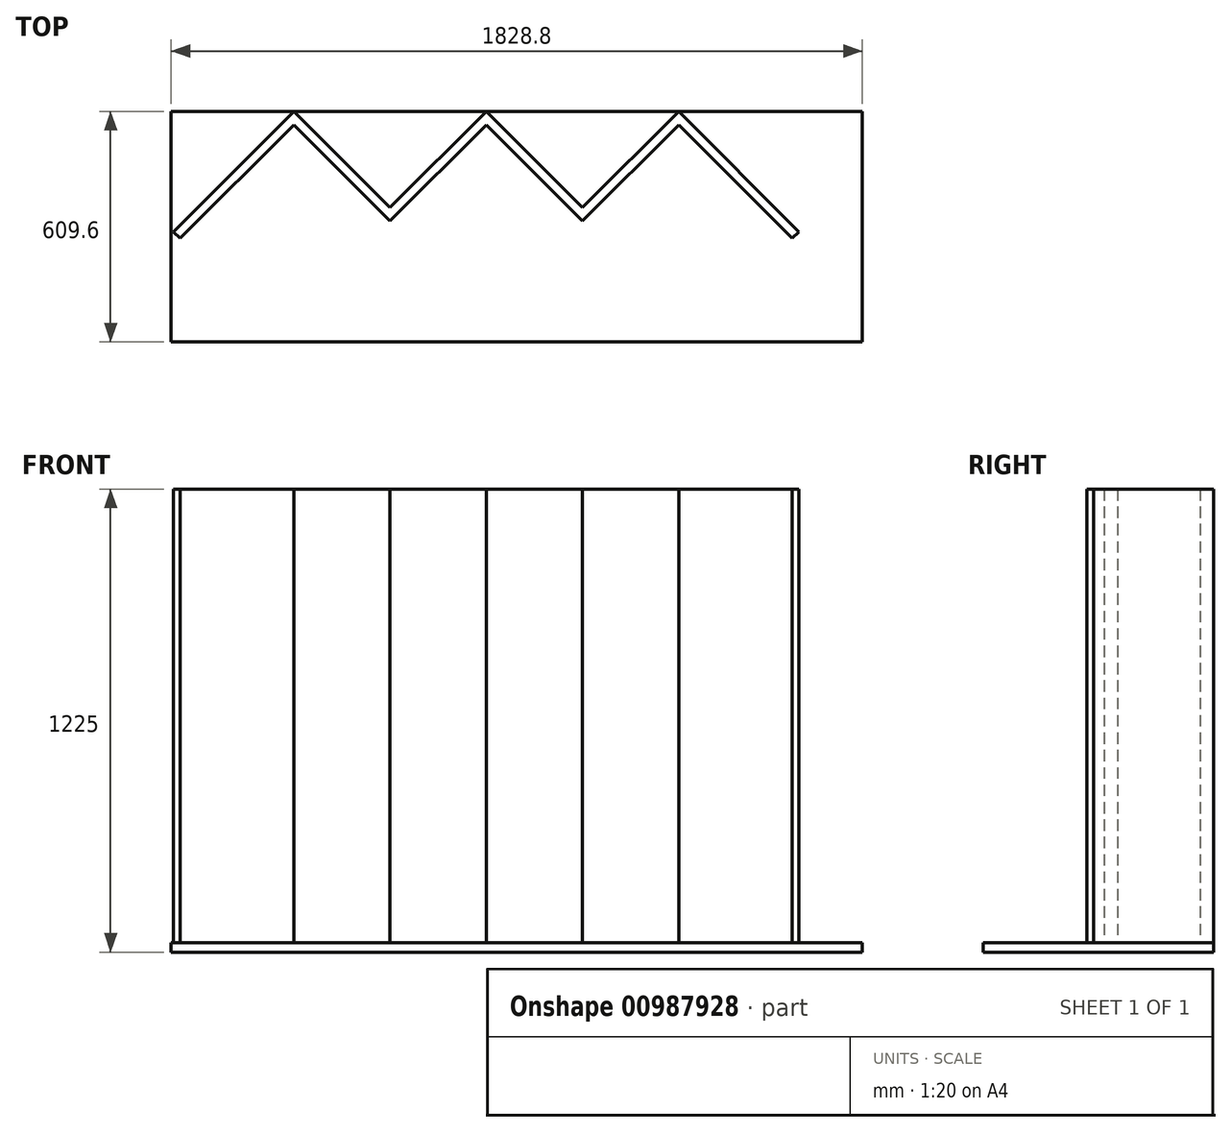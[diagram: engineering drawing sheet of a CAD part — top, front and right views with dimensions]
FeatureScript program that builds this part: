
annotation { "Feature Type Name" : "Feature", "Feature Type Description" : "" }
export const myFeature = defineFeature(function(context is Context, id is Id, definition is map)
    precondition{}
    {
        {
            var Q0;
            Q0=qCreatedBy(makeId("Top.planeOp"),FACE);
            var sketch = newSketch(context, id + "F0", { "sketchPlane" : qUnion([Q0])});
            skLineSegment(sketch, "E0.bottom", {"start": v(914.4, 304.8) * mm, "end": v(-914.4, 304.8) * mm});
            skLineSegment(sketch, "E0.top", {"start": v(914.4, -304.8) * mm, "end": v(-914.4, -304.8) * mm});
            skLineSegment(sketch, "E0.left", {"start": v(914.4, 304.8) * mm, "end": v(914.4, -304.8) * mm});
            skLineSegment(sketch, "E0.right", {"start": v(-914.4, 304.8) * mm, "end": v(-914.4, -304.8) * mm});
            skPoint(sketch, "E0.middle", {"position": v(0, 0) * mm});
            skSolve(sketch);
        }
        {
            var Q0;
            Q0=makeQuery(id+"F0.imprint","IMPRINT",FACE,{"disambiguationData":[TD([[makeQuery(id+"F0.imprint","IMPRINT",EDGE,{"derivedFrom":sQuery(id+"F0.wireOp",EDGE,"E0.bottom")}),1.0]])]});
            extrude(context, id + "F1", {"entities" : qUnion([Q0]), "depth" : 25 * mm, "offsetDistance" : 25 * mm});
        }
        {
            var Q0;
            Q0=makeQuery(id+"F1.opExtrude","CAP_FACE",FACE,{"disambiguationData":[OSD([sQuery(id+"F0.wireOp",EDGE,"E0.bottom"),sQuery(id+"F0.wireOp",EDGE,"E0.top"),sQuery(id+"F0.wireOp",EDGE,"E0.left"),sQuery(id+"F0.wireOp",EDGE,"E0.right")])],"isStart":false});
            var sketch = newSketch(context, id + "F2", { "sketchPlane" : qUnion([Q0])});
            skLineSegment(sketch, "E1", {"start": v(-589.65, 304.8) * mm, "end": v(-335.1, 50.24) * mm});
            skLineSegment(sketch, "E2", {"start": v(-335.1, 50.24) * mm, "end": v(-80.54, 304.8) * mm});
            skLineSegment(sketch, "E3", {"start": v(-80.54, 304.8) * mm, "end": v(174.02, 50.24) * mm});
            skLineSegment(sketch, "E4", {"start": v(174.02, 50.24) * mm, "end": v(428.58, 304.8) * mm});
            skLineSegment(sketch, "E5", {"start": v(428.58, 304.8) * mm, "end": v(746.78, -13.4) * mm});
            skLineSegment(sketch, "E6.1", {"start": v(428.58, 269.44) * mm, "end": v(729.1, -31.08) * mm});
            skLineSegment(sketch, "E6.2", {"start": v(-589.65, 269.44) * mm, "end": v(-335.1, 14.89) * mm});
            skLineSegment(sketch, "E6.3", {"start": v(-335.1, 14.89) * mm, "end": v(-80.54, 269.44) * mm});
            skLineSegment(sketch, "E6.4", {"start": v(-80.54, 269.44) * mm, "end": v(174.02, 14.89) * mm});
            skLineSegment(sketch, "E6.5", {"start": v(174.02, 14.89) * mm, "end": v(428.58, 269.44) * mm});
            skLineSegment(sketch, "E7", {"start": v(729.1, -31.08) * mm, "end": v(746.78, -13.4) * mm});
            skLineSegment(sketch, "E8", {"start": v(-589.65, 304.8) * mm, "end": v(-907.85, -13.4) * mm});
            skLineSegment(sketch, "E9", {"start": v(-589.65, 269.44) * mm, "end": v(-890.17, -31.08) * mm});
            skLineSegment(sketch, "E10", {"start": v(-907.85, -13.4) * mm, "end": v(-890.17, -31.08) * mm});
            skSolve(sketch);
        }
        {
            var Q0;
            Q0=makeQuery(id+"F2.imprint","IMPRINT",FACE,{"disambiguationData":[TD([[makeQuery(id+"F2.imprint","IMPRINT",EDGE,{"derivedFrom":sQuery(id+"F2.wireOp",EDGE,"E1")}),-1.0]])]});
            extrude(context, id + "F3", {"entities" : qUnion([Q0]), "depth" : 1200 * mm, "offsetDistance" : 25 * mm});
        }
    });
